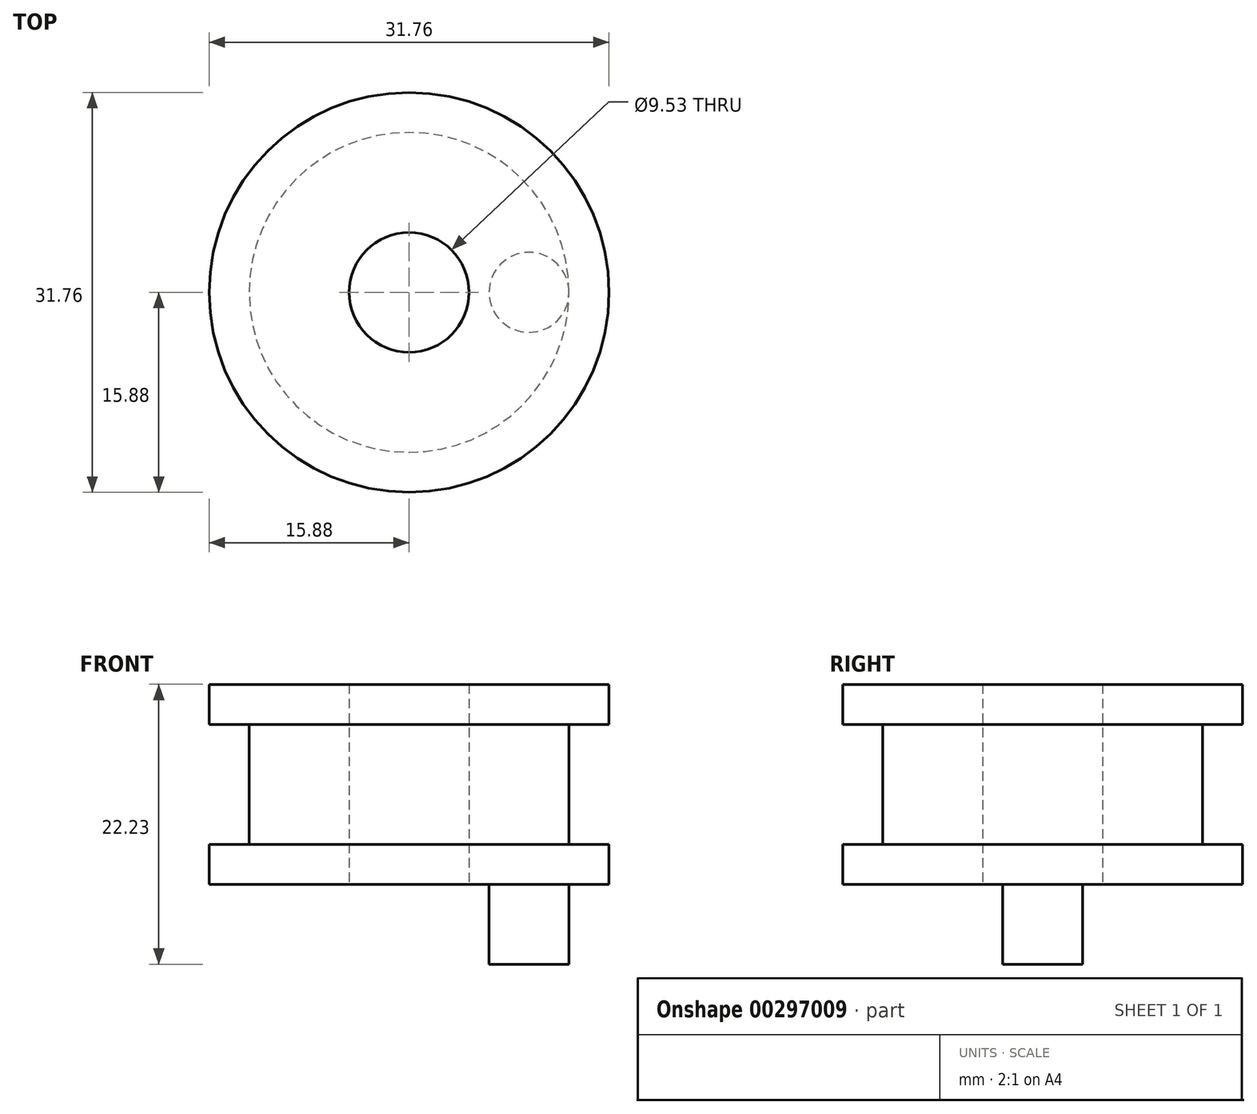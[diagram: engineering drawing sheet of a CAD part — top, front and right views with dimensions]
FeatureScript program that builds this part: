
annotation { "Feature Type Name" : "Feature", "Feature Type Description" : "" }
export const myFeature = defineFeature(function(context is Context, id is Id, definition is map)
    precondition{}
    {
        {
            var Q0;
            Q0=qCreatedBy(makeId("Top.planeOp"),FACE);
            var sketch = newSketch(context, id + "F0", { "sketchPlane" : qUnion([Q0])});
            skCircle(sketch, "E0", {"center": v(0, 0) * mm, "radius": 4.76 * mm});
            skCircle(sketch, "E1", {"center": v(0, 0) * mm, "radius": 12.7 * mm});
            skSolve(sketch);
        }
        {
            var Q0;
            Q0=makeQuery(id+"F0.imprint","IMPRINT",FACE,{"disambiguationData":[TD([[makeQuery(id+"F0.imprint","IMPRINT",EDGE,{"derivedFrom":sQuery(id+"F0.wireOp",EDGE,"E0")}),-1.0]])]});
            extrude(context, id + "F1", {"entities" : qUnion([Q0]), "depth" : 12.7 * mm});
        }
        {
            var Q0;
            Q0=makeQuery(id+"F1.opExtrude","CAP_FACE",FACE,{"disambiguationData":[OSD([sQuery(id+"F0.wireOp",EDGE,"E0"),sQuery(id+"F0.wireOp",EDGE,"E1")])],"isStart":false});
            var sketch = newSketch(context, id + "F2", { "sketchPlane" : qUnion([Q0])});
            skCircle(sketch, "E2", {"center": v(0, 0) * mm, "radius": 15.88 * mm});
            skCircle(sketch, "E3", {"center": v(0, 0) * mm, "radius": 4.76 * mm});
            skSolve(sketch);
        }
        {
            var Q0;
            Q0 = qSketchRegion(id + "F2", true);
            extrude(context, id + "F3", {"entities" : qUnion([Q0]), "operationType" : NewBodyOperationType.ADD, "depth" : 3.17 * mm});
        }
        {
            var Q0;
            Q0=qCreatedBy(makeId("Top.planeOp"),FACE);
            var sketch = newSketch(context, id + "F4", { "sketchPlane" : qUnion([Q0])});
            skCircle(sketch, "E4", {"center": v(0, 0) * mm, "radius": 4.76 * mm});
            skCircle(sketch, "E5", {"center": v(0, 0) * mm, "radius": 15.88 * mm});
            skSolve(sketch);
        }
        {
            var Q0;
            Q0=makeQuery(id+"F4.imprint","IMPRINT",FACE,{"disambiguationData":[TD([[makeQuery(id+"F4.imprint","IMPRINT",EDGE,{"derivedFrom":sQuery(id+"F4.wireOp",EDGE,"E4")}),-1.0]])]});
            extrude(context, id + "F5", {"entities" : qUnion([Q0]), "operationType" : NewBodyOperationType.ADD, "depth" : 3.17 * mm});
        }
        {
            var Q0;
            Q0=makeQuery(id+"F5.boolean.opBoolean","MERGE",FACE,{"derivedFrom":[makeQuery(id+"F1.opExtrude","CAP_FACE",FACE,{"disambiguationData":[OSD([sQuery(id+"F0.wireOp",EDGE,"E0"),sQuery(id+"F0.wireOp",EDGE,"E1")])],"isStart":true}),makeQuery(id+"F5.opExtrude","CAP_FACE",FACE,{"disambiguationData":[OSD([sQuery(id+"F4.wireOp",EDGE,"E4"),sQuery(id+"F4.wireOp",EDGE,"E5")])],"isStart":true})]});
            var sketch = newSketch(context, id + "F6", { "sketchPlane" : qUnion([Q0])});
            skCircle(sketch, "E6", {"center": v(9.53, 0) * mm, "radius": 3.18 * mm});
            skSolve(sketch);
        }
        {
            var Q0;
            Q0=makeQuery(id+"F6.imprint","IMPRINT",FACE,{"disambiguationData":[TD([[makeQuery(id+"F6.imprint","IMPRINT",EDGE,{"derivedFrom":sQuery(id+"F6.wireOp",EDGE,"E6")}),1.0]])]});
            extrude(context, id + "F7", {"entities" : qUnion([Q0]), "operationType" : NewBodyOperationType.ADD, "depth" : 6.35 * mm});
        }
    });
